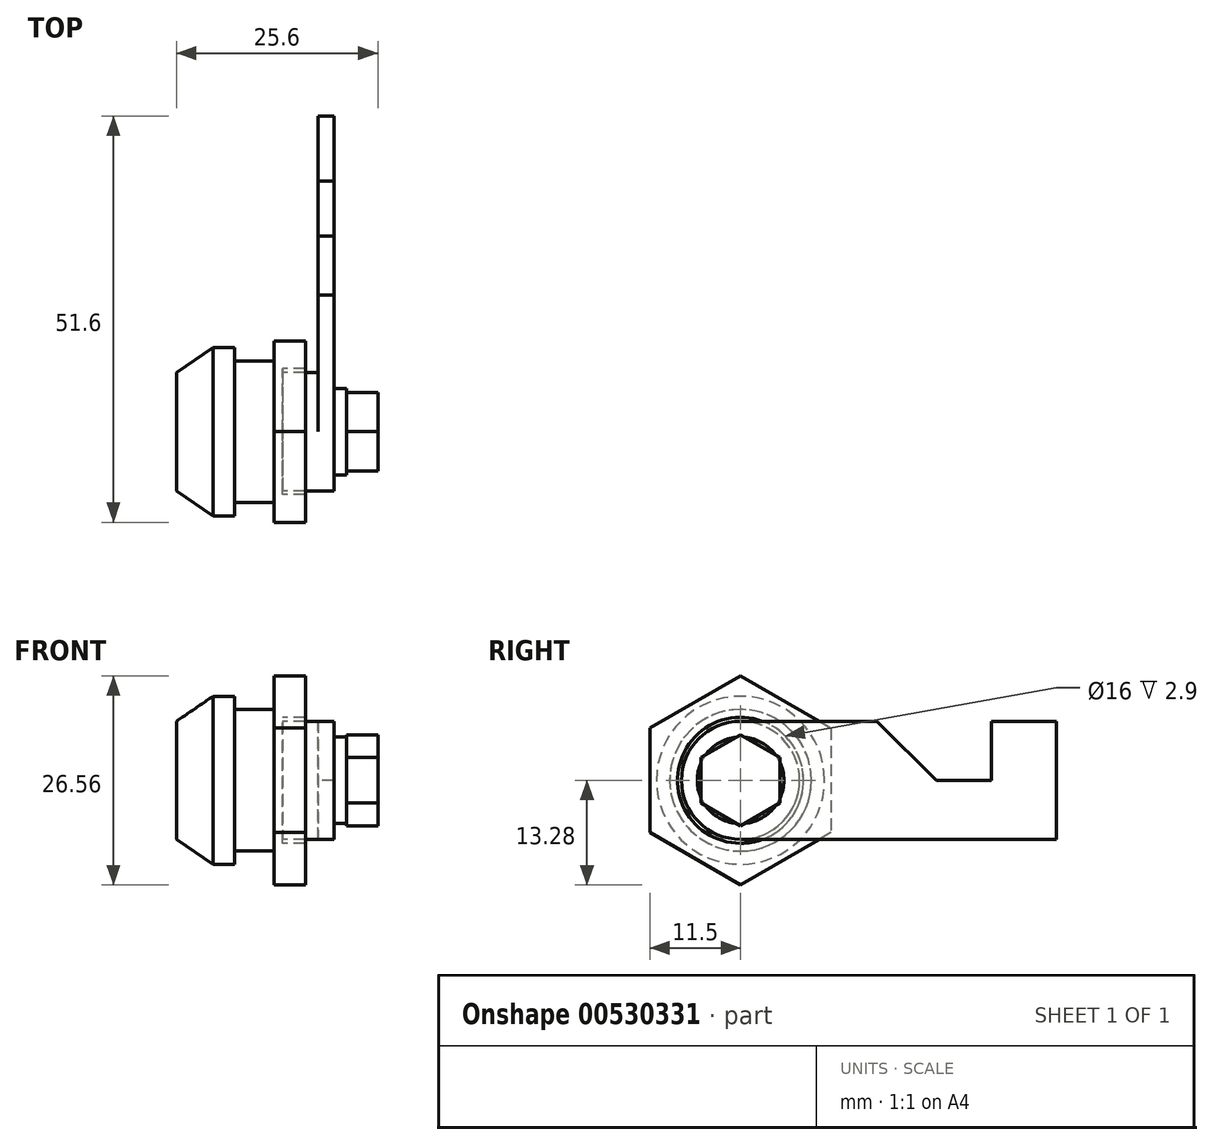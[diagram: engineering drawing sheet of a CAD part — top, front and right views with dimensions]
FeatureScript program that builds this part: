
annotation { "Feature Type Name" : "Feature", "Feature Type Description" : "" }
export const myFeature = defineFeature(function(context is Context, id is Id, definition is map)
    precondition{}
    {
        {
            var Q0;
            Q0=qCreatedBy(makeId("Front.planeOp"),FACE);
            var sketch = newSketch(context, id + "F0", { "sketchPlane" : qUnion([Q0])});
            skLineSegment(sketch, "E0", {"start": v(0, 0) * mm, "end": v(21.6, 0) * mm});
            skLineSegment(sketch, "E1", {"start": v(0, 0) * mm, "end": v(0, 7.5) * mm});
            skLineSegment(sketch, "E2", {"start": v(0, 7.5) * mm, "end": v(4.65, 10.68) * mm});
            skLineSegment(sketch, "E3", {"start": v(4.65, 10.68) * mm, "end": v(7.4, 10.68) * mm});
            skLineSegment(sketch, "E4", {"start": v(7.4, 10.68) * mm, "end": v(7.4, 9) * mm});
            skLineSegment(sketch, "E5", {"start": v(7.4, 9) * mm, "end": v(13.5, 9) * mm});
            skLineSegment(sketch, "E6", {"start": v(13.5, 9) * mm, "end": v(13.5, 7.5) * mm});
            skLineSegment(sketch, "E7", {"start": v(13.5, 7.5) * mm, "end": v(20, 7.5) * mm});
            skLineSegment(sketch, "E8", {"start": v(20, 7.5) * mm, "end": v(20, 5.5) * mm});
            skLineSegment(sketch, "E9", {"start": v(20, 5.5) * mm, "end": v(21.6, 5.5) * mm});
            skLineSegment(sketch, "E10", {"start": v(21.6, 5.5) * mm, "end": v(21.6, 0) * mm});
            skSolve(sketch);
        }
        {
            var Q0;
            Q0 = qSketchRegion(id + "F0", true);
            var Q1;
            Q1=sQuery(id+"F0.wireOp",EDGE,"E0");
            revolve(context, id + "F1", {"surfaceOperationType" : NewSurfaceOperationType.NEW, "entities" : qUnion([Q0]), "axis" : qUnion([Q1]), "revolveType" : RevolveType.FULL});
        }
        {
            assignVariable(context, id + "F2", {"variableType" : VariableType.LENGTH, "name" : "d", "lengthValue" : 5 * mm});
        }
        {
            var Q0;
            Q0=makeQuery(id+"F1.opRevolve","SWEPT_FACE",FACE,{"disambiguationData":[OSD([sQuery(id+"F0.wireOp",EDGE,"E4")])]});
            cPlane(context, id + "F3", {"entities" : qUnion([Q0]), "cplaneType" : CPlaneType.OFFSET, "offset" : getVariable(context, 'd'), "width" : 150 * mm, "height" : 150 * mm});
        }
        {
            var Q0;
            Q0=qCreatedBy(id+"F3.planeOp",FACE);
            var sketch = newSketch(context, id + "F4", { "sketchPlane" : qUnion([Q0])});
            skCircle(sketch, "E11.cCircle", {"center": v(0, 0) * mm, "radius": 11.5 * mm, "construction": true});
            skLineSegment(sketch, "E11.0", {"start": v(0, 13.28) * mm, "end": v(11.5, 6.64) * mm});
            skLineSegment(sketch, "E11.1", {"start": v(11.5, 6.64) * mm, "end": v(11.5, -6.64) * mm});
            skLineSegment(sketch, "E11.2", {"start": v(11.5, -6.64) * mm, "end": v(0, -13.28) * mm});
            skLineSegment(sketch, "E11.3", {"start": v(0, -13.28) * mm, "end": v(-11.5, -6.64) * mm});
            skLineSegment(sketch, "E11.4", {"start": v(-11.5, -6.64) * mm, "end": v(-11.5, 6.64) * mm});
            skLineSegment(sketch, "E11.5", {"start": v(-11.5, 6.64) * mm, "end": v(0, 13.28) * mm});
            skPoint(sketch, "E11.0.midPoint", {"position": v(5.75, 9.96) * mm});
            skCircle(sketch, "E12", {"center": v(0, 0) * mm, "radius": 8 * mm});
            skSolve(sketch);
        }
        {
            var Q0;
            Q0 = qSketchRegion(id + "F4", true);
            extrude(context, id + "F5", {"entities" : qUnion([Q0]), "operationType" : NewBodyOperationType.ADD, "depth" : 4 * mm, "offsetDistance" : 25 * mm});
        }
        {
            var Q0;
            Q0=makeQuery(id+"F1.opRevolve","SWEPT_FACE",FACE,{"disambiguationData":[OSD([sQuery(id+"F0.wireOp",EDGE,"E8")])]});
            var sketch = newSketch(context, id + "F6", { "sketchPlane" : qUnion([Q0])});
            skArc(sketch, "E13.0", {"start": v(0, 7.5) * mm, "mid": v(-7.5, 0) * mm, "end": v(0, -7.5) * mm});
            skLineSegment(sketch, "E14", {"start": v(0, 7.5) * mm, "end": v(40.1, 7.5) * mm});
            skLineSegment(sketch, "E15", {"start": v(40.1, 7.5) * mm, "end": v(40.1, -7.5) * mm});
            skLineSegment(sketch, "E16", {"start": v(40.1, -7.5) * mm, "end": v(0, -7.5) * mm});
            skSolve(sketch);
        }
        {
            var Q0;
            Q0 = qSketchRegion(id + "F6", true);
            extrude(context, id + "F7", {"entities" : qUnion([Q0]), "operationType" : NewBodyOperationType.ADD, "oppositeDirection" : true, "depth" : 2 * mm, "offsetDistance" : 25 * mm});
        }
        {
            var Q0;
            Q0=makeQuery(id+"F1.opRevolve","SWEPT_FACE",FACE,{"disambiguationData":[OSD([sQuery(id+"F0.wireOp",EDGE,"E10")])]});
            var sketch = newSketch(context, id + "F8", { "sketchPlane" : qUnion([Q0])});
            skCircle(sketch, "E17.cCircle", {"center": v(0, 0) * mm, "radius": 5 * mm, "construction": true});
            skLineSegment(sketch, "E17.0", {"start": v(5, 2.89) * mm, "end": v(5, -2.89) * mm});
            skLineSegment(sketch, "E17.1", {"start": v(5, -2.89) * mm, "end": v(0, -5.77) * mm});
            skLineSegment(sketch, "E17.2", {"start": v(0, -5.77) * mm, "end": v(-5, -2.89) * mm});
            skLineSegment(sketch, "E17.3", {"start": v(-5, -2.89) * mm, "end": v(-5, 2.89) * mm});
            skLineSegment(sketch, "E17.4", {"start": v(-5, 2.89) * mm, "end": v(0, 5.77) * mm});
            skLineSegment(sketch, "E17.5", {"start": v(0, 5.77) * mm, "end": v(5, 2.89) * mm});
            skPoint(sketch, "E17.0.midPoint", {"position": v(5, 0) * mm});
            skSolve(sketch);
        }
        {
            var Q0;
            Q0 = qSketchRegion(id + "F8", true);
            extrude(context, id + "F9", {"entities" : qUnion([Q0]), "operationType" : NewBodyOperationType.ADD, "depth" : 4 * mm, "offsetDistance" : 25 * mm});
        }
        {
            var Q0;
            Q0=makeQuery(id+"F7.opExtrude","CAP_FACE",FACE,{"disambiguationData":[OSD([sQuery(id+"F6.wireOp",EDGE,"E13.0"),sQuery(id+"F6.wireOp",EDGE,"E14"),sQuery(id+"F6.wireOp",EDGE,"E15"),sQuery(id+"F6.wireOp",EDGE,"E16")])],"isStart":false});
            var sketch = newSketch(context, id + "F10", { "sketchPlane" : qUnion([Q0])});
            skLineSegment(sketch, "E18", {"start": v(-31.85, 7.5) * mm, "end": v(-31.85, 0) * mm});
            skLineSegment(sketch, "E19", {"start": v(-31.85, 0) * mm, "end": v(-24.85, 0) * mm});
            skLineSegment(sketch, "E20", {"start": v(-24.85, 0) * mm, "end": v(-17.35, 7.5) * mm});
            skLineSegment(sketch, "E21", {"start": v(-31.85, 7.5) * mm, "end": v(-17.35, 7.5) * mm});
            skSolve(sketch);
        }
        {
            var Q0;
            Q0 = qSketchRegion(id + "F10", true);
            extrude(context, id + "F11", {"entities" : qUnion([Q0]), "operationType" : NewBodyOperationType.REMOVE, "oppositeDirection" : true, "depth" : 25 * mm, "offsetDistance" : 25 * mm});
        }
    });
